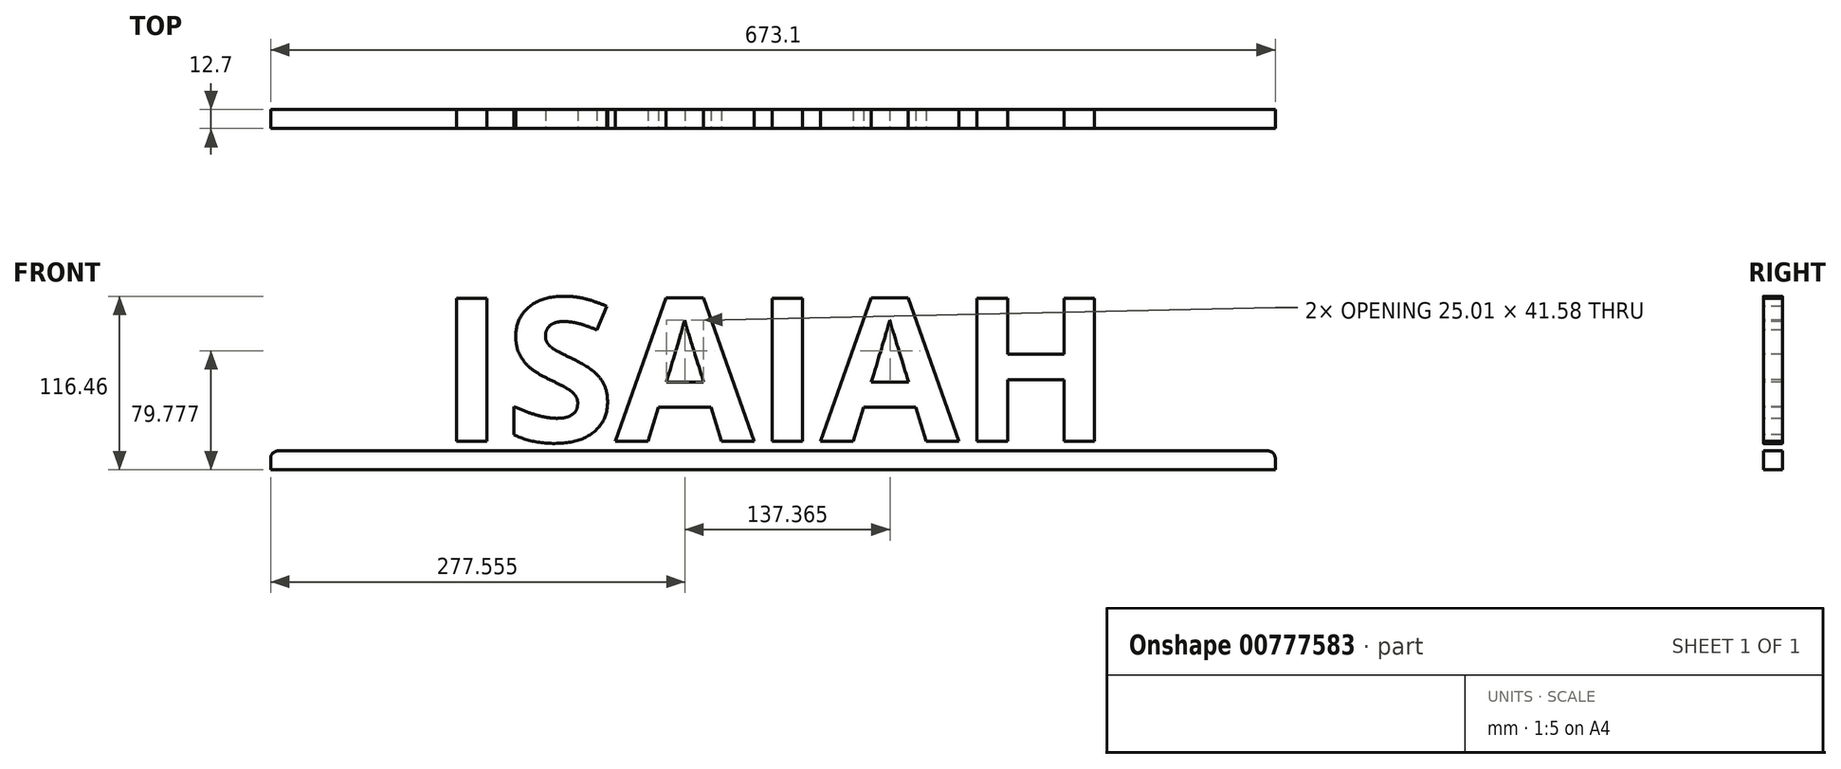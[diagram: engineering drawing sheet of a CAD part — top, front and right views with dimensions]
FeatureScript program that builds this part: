
annotation { "Feature Type Name" : "Feature", "Feature Type Description" : "" }
export const myFeature = defineFeature(function(context is Context, id is Id, definition is map)
    precondition{}
    {
        {
            var Q0;
            Q0=qCreatedBy(makeId("Front.planeOp"),FACE);
            var sketch = newSketch(context, id + "F0", { "sketchPlane" : qUnion([Q0])});
            skLineSegment(sketch, "E0.bottom", {"start": v(-336.55, -18.8) * mm, "end": v(336.55, -18.8) * mm});
            skLineSegment(sketch, "E0.top", {"start": v(-336.55, -31.5) * mm, "end": v(336.55, -31.5) * mm});
            skLineSegment(sketch, "E0.left", {"start": v(-336.55, -18.8) * mm, "end": v(-336.55, -31.5) * mm});
            skLineSegment(sketch, "E0.right", {"start": v(336.55, -18.8) * mm, "end": v(336.55, -31.5) * mm});
            skPoint(sketch, "E1", {"position": v(0, -18.8) * mm});
            skPoint(sketch, "E2", {"position": v(0, -31.5) * mm});
            skSolve(sketch);
        }
        {
            var Q0;
            Q0=makeQuery(id+"F0.imprint","IMPRINT",FACE,{"disambiguationData":[TD([[makeQuery(id+"F0.imprint","IMPRINT",EDGE,{"derivedFrom":sQuery(id+"F0.wireOp",EDGE,"E0.bottom")}),-1.0]])]});
            extrude(context, id + "F1", {"entities" : qUnion([Q0]), "depth" : 12.7 * mm, "offsetDistance" : 25.4 * mm});
        }
        {
            var Q0;
            Q0=makeQuery(id+"F1.opExtrude","CAP_FACE",FACE,{"disambiguationData":[OSD([sQuery(id+"F0.wireOp",EDGE,"E0.bottom"),sQuery(id+"F0.wireOp",EDGE,"E0.top"),sQuery(id+"F0.wireOp",EDGE,"E0.left"),sQuery(id+"F0.wireOp",EDGE,"E0.right")])],"isStart":false});
            var sketch = newSketch(context, id + "F2", { "sketchPlane" : qUnion([Q0])});
            skText(sketch, "E3", { "text": "ISAIAH", "fontName": "OpenSans-Bold.ttf"});
            const initialGuessF2  = {"E3": [-0.22417, -0.01245, 1, 0, 0.09686]};
            skSetInitialGuess(sketch, initialGuessF2);
            skSolve(sketch);
        }
        {
            var Q0;
            Q0 = qSketchRegion(id + "F2", true);
            extrude(context, id + "F3", {"entities" : qUnion([Q0]), "operationType" : NewBodyOperationType.ADD, "depth" : -12.7 * mm, "offsetDistance" : 25.4 * mm});
        }
        {
            var Q0;
            Q0=makeQuery(id+"F1.opExtrude","SWEPT_EDGE",EDGE,{"disambiguationData":[OSD([sQuery(id+"F0.wireOp",EDGE,"E0.bottom"),sQuery(id+"F0.wireOp",EDGE,"E0.right")])]});
            var Q1;
            Q1=makeQuery(id+"F1.opExtrude","SWEPT_EDGE",EDGE,{"disambiguationData":[OSD([sQuery(id+"F0.wireOp",EDGE,"E0.bottom"),sQuery(id+"F0.wireOp",EDGE,"E0.left")])]});
            fillet(context, id + "F4", {"entities" : qUnion([Q0, Q1]), "radius" : 5.08 * mm, "tangentPropagation" : true, "allowEdgeOverflow" : false});
        }
    });
